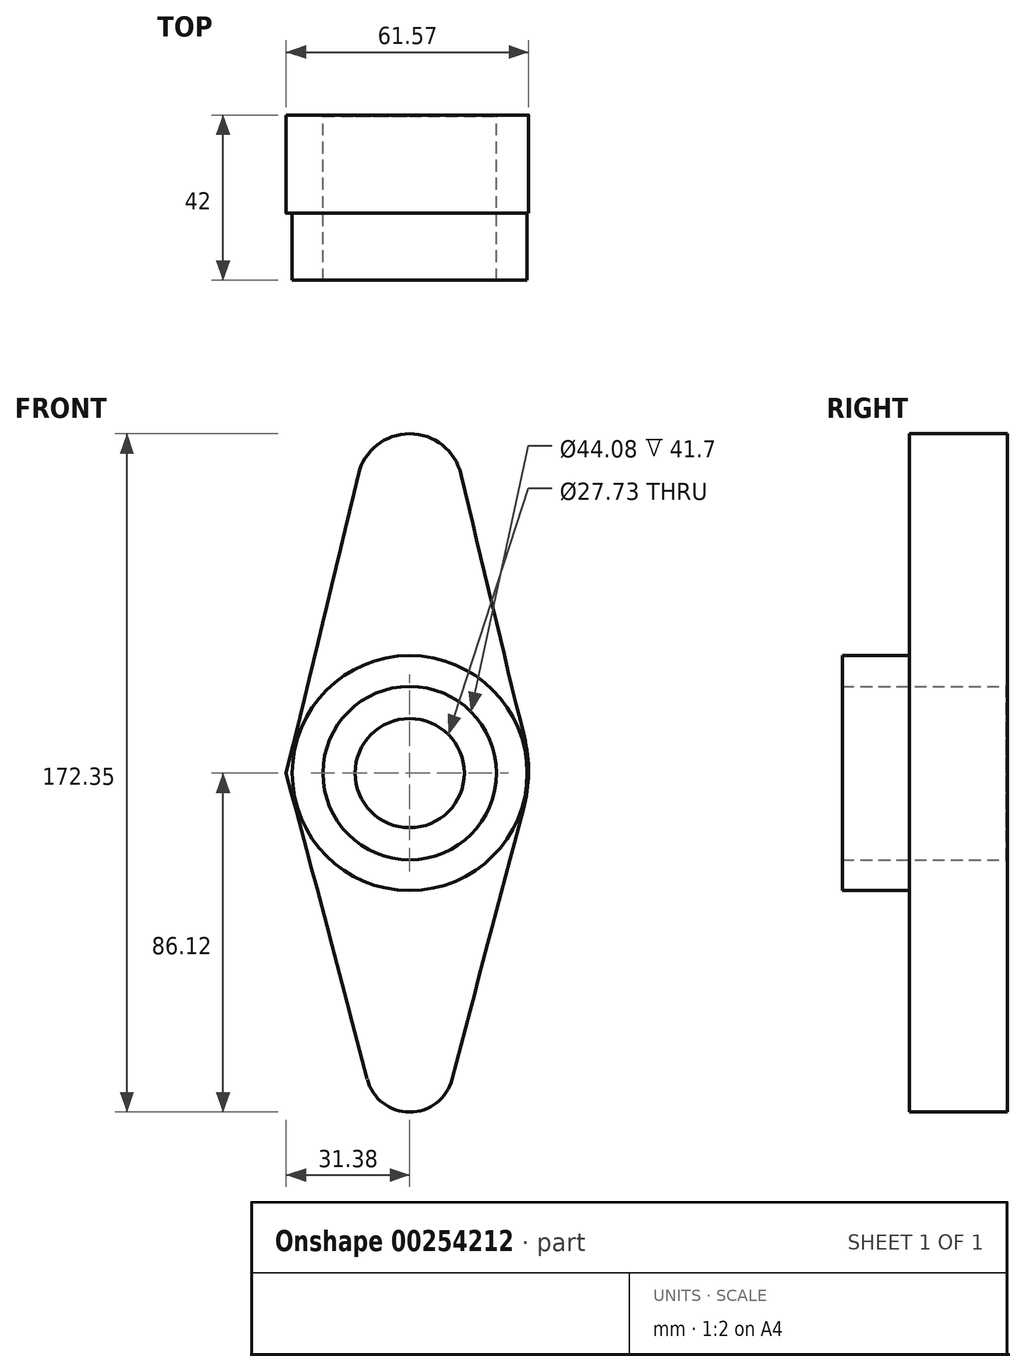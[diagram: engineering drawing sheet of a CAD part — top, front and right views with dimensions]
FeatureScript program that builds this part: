
annotation { "Feature Type Name" : "Feature", "Feature Type Description" : "" }
export const myFeature = defineFeature(function(context is Context, id is Id, definition is map)
    precondition{}
    {
        {
            var Q0;
            Q0=qCreatedBy(makeId("Front.planeOp"),FACE);
            var sketch = newSketch(context, id + "F0", { "sketchPlane" : qUnion([Q0])});
            skCircle(sketch, "E0", {"center": v(0, 72.81) * mm, "radius": 13.41 * mm});
            skCircle(sketch, "E1", {"center": v(0, 0) * mm, "radius": 29.84 * mm});
            skCircle(sketch, "E2", {"center": v(0, -75) * mm, "radius": 11.12 * mm});
            skLineSegment(sketch, "E3", {"start": v(-13.41, 72.81) * mm, "end": v(-31.39, 0) * mm});
            skLineSegment(sketch, "E4", {"start": v(-31.39, 0) * mm, "end": v(-11.12, -75) * mm});
            skLineSegment(sketch, "E5", {"start": v(11.12, -75) * mm, "end": v(31.39, 0) * mm});
            skLineSegment(sketch, "E6", {"start": v(31.39, 0) * mm, "end": v(13.41, 72.81) * mm});
            skCircle(sketch, "E7", {"center": v(0, 0) * mm, "radius": 22.04 * mm});
            skCircle(sketch, "E8", {"center": v(0, 0) * mm, "radius": 13.87 * mm});
            skSolve(sketch);
        }
        {
            var Q0;
            Q0=makeQuery(id+"F0.imprint","IMPRINT",FACE,{"disambiguationData":[TD([[makeQuery(id+"F0.imprint","IMPRINT",EDGE,{"derivedFrom":sQuery(id+"F0.wireOp",EDGE,"0uHNPh89-aWxb-NHOG-xwbp-gSGj1il5x9TW")}),1.0]])]});
            var Q1;
            Q1=makeQuery(id+"F0.imprint","IMPRINT",FACE,{"disambiguationData":[TD([[makeQuery(id+"F0.imprint","IMPRINT",EDGE,{"derivedFrom":sQuery(id+"F0.wireOp",EDGE,"0uHNPh89-aWxb-NHOG-xwbp-gSGj1il5x9TW")}),-1.0]])]});
            var Q2;
            {var subQ0=sQuery(id+"F0.wireOp",EDGE,"z7gx10TJ-BllW-q8bY-S4K0-FxVff8viO4pO");var subQ1=sQuery(id+"F0.wireOp",EDGE,"E0");var subQ2=makeQuery(id+"F0.imprint","INTERSECT",VERTEX,{"derivedFrom":[subQ1,subQ0]});Q2=makeQuery(id+"F0.imprint","IMPRINT",FACE,{"disambiguationData":[TD([[makeQuery(id+"F0.imprint","IMPRINT",EDGE,{"disambiguationData":[TD([[subQ2,-1.0]])],"derivedFrom":subQ1}),-1.0]])]});}
            var Q3;
            {var subQ0=sQuery(id+"F0.wireOp",EDGE,"SLZA87bq-c7lT-pN1u-qhHm-x7yccJrzVBUm");var subQ1=sQuery(id+"F0.wireOp",EDGE,"E1");var subQ2=makeQuery(id+"F0.imprint","INTERSECT",VERTEX,{"derivedFrom":[subQ1,subQ0]});Q3=makeQuery(id+"F0.imprint","IMPRINT",FACE,{"disambiguationData":[TD([[makeQuery(id+"F0.imprint","IMPRINT",EDGE,{"disambiguationData":[TD([[subQ2,-1.0]])],"derivedFrom":subQ1}),-1.0]])]});}
            var Q4;
            {var subQ0=sQuery(id+"F0.wireOp",EDGE,"E2");var subQ1=makeQuery(id+"F0.imprint","INTERSECT",VERTEX,{"derivedFrom":[subQ0,sQuery(id+"F0.wireOp",EDGE,"8I14K3XJ-zyX1-hXYv-A3UP-ttUHuBeU514k")]});Q4=makeQuery(id+"F0.imprint","IMPRINT",FACE,{"disambiguationData":[TD([[makeQuery(id+"F0.imprint","IMPRINT",EDGE,{"disambiguationData":[TD([[subQ1,1.0]])],"derivedFrom":subQ0}),1.0]])]});}
            var Q5;
            {var subQ0=sQuery(id+"F0.wireOp",EDGE,"E0");var subQ1=makeQuery(id+"F0.imprint","INTERSECT",VERTEX,{"derivedFrom":[subQ0,sQuery(id+"F0.wireOp",EDGE,"z7gx10TJ-BllW-q8bY-S4K0-FxVff8viO4pO")]});Q5=makeQuery(id+"F0.imprint","IMPRINT",FACE,{"disambiguationData":[TD([[makeQuery(id+"F0.imprint","IMPRINT",EDGE,{"disambiguationData":[TD([[subQ1,1.0]])],"derivedFrom":subQ0}),1.0]])]});}
            extrude(context, id + "F1", {"entities" : qUnion([Q0, Q1, Q2, Q3, Q4, Q5]), "depth" : 1 * mm});
        }
        {
            var Q0;
            Q0 = qSketchRegion(id + "F0", true);
            extrude(context, id + "F2", {"entities" : qUnion([Q0]), "operationType" : NewBodyOperationType.ADD, "depth" : 25 * mm});
        }
        {
            var Q0;
            Q0 = qSketchRegion(id + "F0", true);
            extrude(context, id + "F3", {"entities" : qUnion([Q0]), "operationType" : NewBodyOperationType.ADD, "depth" : 25 * mm});
        }
        {
            var Q0;
            Q0=makeQuery(id+"F0.imprint","IMPRINT",FACE,{"disambiguationData":[TD([[makeQuery(id+"F0.imprint","IMPRINT",EDGE,{"derivedFrom":sQuery(id+"F0.wireOp",EDGE,"E1")}),1.0]])]});
            extrude(context, id + "F4", {"entities" : qUnion([Q0]), "operationType" : NewBodyOperationType.ADD, "depth" : 42 * mm});
        }
        {
            var Q0;
            Q0=sQuery(id+"F0.wireOp",EDGE,"E8");
            extrude(context, id + "F5", {"bodyType" : ToolBodyType.SURFACE, "surfaceEntities" : qUnion([Q0]), "oppositeDirection" : true, "depth" : 1 * mm});
        }
        {
            var Q0;
            Q0=makeQuery(id+"F0.imprint","IMPRINT",FACE,{"disambiguationData":[TD([[makeQuery(id+"F0.imprint","IMPRINT",EDGE,{"derivedFrom":sQuery(id+"F0.wireOp",EDGE,"E7")}),1.0]])]});
            extrude(context, id + "F6", {"entities" : qUnion([Q0]), "operationType" : NewBodyOperationType.ADD, "depth" : 0.3 * mm});
        }
        {
            var Q0;
            {var subQ0=sQuery(id+"F0.wireOp",EDGE,"E6");var subQ1=sQuery(id+"F0.wireOp",EDGE,"E0");Q0=makeQuery(id+"F2.boolean.opBoolean","MERGE",EDGE,{"derivedFrom":[makeQuery(id+"F1.opExtrude","SWEPT_EDGE",EDGE,{"disambiguationData":[OSD([subQ1,subQ0])]}),makeQuery(id+"F2.opExtrude","SWEPT_EDGE",EDGE,{"disambiguationData":[OSD([subQ1,subQ0])]})]});}
            fillet(context, id + "F7", {"entities" : qUnion([Q0]), "radius" : 6747.37 * mm, "tangentPropagation" : true, "allowEdgeOverflow" : false});
        }
        {
            var Q0;
            {var subQ0=sQuery(id+"F0.wireOp",EDGE,"E3");var subQ1=sQuery(id+"F0.wireOp",EDGE,"E0");Q0=makeQuery(id+"F2.boolean.opBoolean","MERGE",EDGE,{"derivedFrom":[makeQuery(id+"F1.opExtrude","SWEPT_EDGE",EDGE,{"disambiguationData":[OSD([subQ1,subQ0])]}),makeQuery(id+"F2.opExtrude","SWEPT_EDGE",EDGE,{"disambiguationData":[OSD([subQ1,subQ0])]})]});}
            fillet(context, id + "F8", {"entities" : qUnion([Q0]), "radius" : 9058.47 * mm, "tangentPropagation" : true, "allowEdgeOverflow" : false});
        }
        {
            var Q0;
            {var subQ0=sQuery(id+"F0.wireOp",EDGE,"E4");var subQ1=sQuery(id+"F0.wireOp",EDGE,"E3");var subQ2=sQuery(id+"F0.wireOp",EDGE,"E0");Q0=makeQuery(id+"F8.opFillet","BLEND_EDGE",EDGE,{"blendedFrom":[makeQuery(id+"F2.boolean.opBoolean","MERGE",EDGE,{"derivedFrom":[makeQuery(id+"F1.opExtrude","SWEPT_EDGE",EDGE,{"disambiguationData":[OSD([subQ2,subQ1])]}),makeQuery(id+"F2.opExtrude","SWEPT_EDGE",EDGE,{"disambiguationData":[OSD([subQ2,subQ1])]})]}),makeQuery(id+"F2.boolean.opBoolean","MERGE",FACE,{"derivedFrom":[makeQuery(id+"F1.opExtrude","SWEPT_FACE",FACE,{"disambiguationData":[OSD([subQ0])]}),makeQuery(id+"F2.opExtrude","SWEPT_FACE",FACE,{"disambiguationData":[OSD([subQ0])]})]})],"blendedInto":[makeQuery(id+"F2.boolean.opBoolean","MERGE",FACE,{"derivedFrom":[makeQuery(id+"F1.opExtrude","SWEPT_FACE",FACE,{"disambiguationData":[OSD([subQ0])]}),makeQuery(id+"F2.opExtrude","SWEPT_FACE",FACE,{"disambiguationData":[OSD([subQ0])]})]})]});}
            fillet(context, id + "F9", {"entities" : qUnion([Q0]), "radius" : 0.24 * mm, "tangentPropagation" : true, "allowEdgeOverflow" : false});
        }
        {
            var Q0;
            {var subQ0=sQuery(id+"F0.wireOp",EDGE,"E5");var subQ1=sQuery(id+"F0.wireOp",EDGE,"E2");Q0=makeQuery(id+"F2.boolean.opBoolean","MERGE",EDGE,{"derivedFrom":[makeQuery(id+"F1.opExtrude","SWEPT_EDGE",EDGE,{"disambiguationData":[OSD([subQ1,subQ0])]}),makeQuery(id+"F2.opExtrude","SWEPT_EDGE",EDGE,{"disambiguationData":[OSD([subQ1,subQ0])]})]});}
            fillet(context, id + "F10", {"entities" : qUnion([Q0]), "radius" : 15012.22 * mm, "tangentPropagation" : true, "allowEdgeOverflow" : false});
        }
        {
            var Q0;
            {var subQ0=sQuery(id+"F0.wireOp",EDGE,"E4");var subQ1=sQuery(id+"F0.wireOp",EDGE,"E2");Q0=makeQuery(id+"F2.boolean.opBoolean","MERGE",EDGE,{"derivedFrom":[makeQuery(id+"F1.opExtrude","SWEPT_EDGE",EDGE,{"disambiguationData":[OSD([subQ1,subQ0])]}),makeQuery(id+"F2.opExtrude","SWEPT_EDGE",EDGE,{"disambiguationData":[OSD([subQ1,subQ0])]})]});}
            fillet(context, id + "F11", {"entities" : qUnion([Q0]), "radius" : 12028.03 * mm, "tangentPropagation" : true, "allowEdgeOverflow" : false});
        }
        {
            var Q0;
            {var subQ0=sQuery(id+"F0.wireOp",EDGE,"E6");var subQ1=sQuery(id+"F0.wireOp",EDGE,"E5");var subQ2=sQuery(id+"F0.wireOp",EDGE,"E2");Q0=makeQuery(id+"F10.opFillet","BLEND_EDGE",EDGE,{"blendedFrom":[makeQuery(id+"F2.boolean.opBoolean","MERGE",EDGE,{"derivedFrom":[makeQuery(id+"F1.opExtrude","SWEPT_EDGE",EDGE,{"disambiguationData":[OSD([subQ2,subQ1])]}),makeQuery(id+"F2.opExtrude","SWEPT_EDGE",EDGE,{"disambiguationData":[OSD([subQ2,subQ1])]})]}),makeQuery(id+"F2.boolean.opBoolean","MERGE",FACE,{"derivedFrom":[makeQuery(id+"F1.opExtrude","SWEPT_FACE",FACE,{"disambiguationData":[OSD([subQ0])]}),makeQuery(id+"F2.opExtrude","SWEPT_FACE",FACE,{"disambiguationData":[OSD([subQ0])]})]})],"blendedInto":[makeQuery(id+"F2.boolean.opBoolean","MERGE",FACE,{"derivedFrom":[makeQuery(id+"F1.opExtrude","SWEPT_FACE",FACE,{"disambiguationData":[OSD([subQ0])]}),makeQuery(id+"F2.opExtrude","SWEPT_FACE",FACE,{"disambiguationData":[OSD([subQ0])]})]})]});}
            fillet(context, id + "F12", {"entities" : qUnion([Q0]), "radius" : 36.83 * mm, "tangentPropagation" : true, "allowEdgeOverflow" : false});
        }
    });
